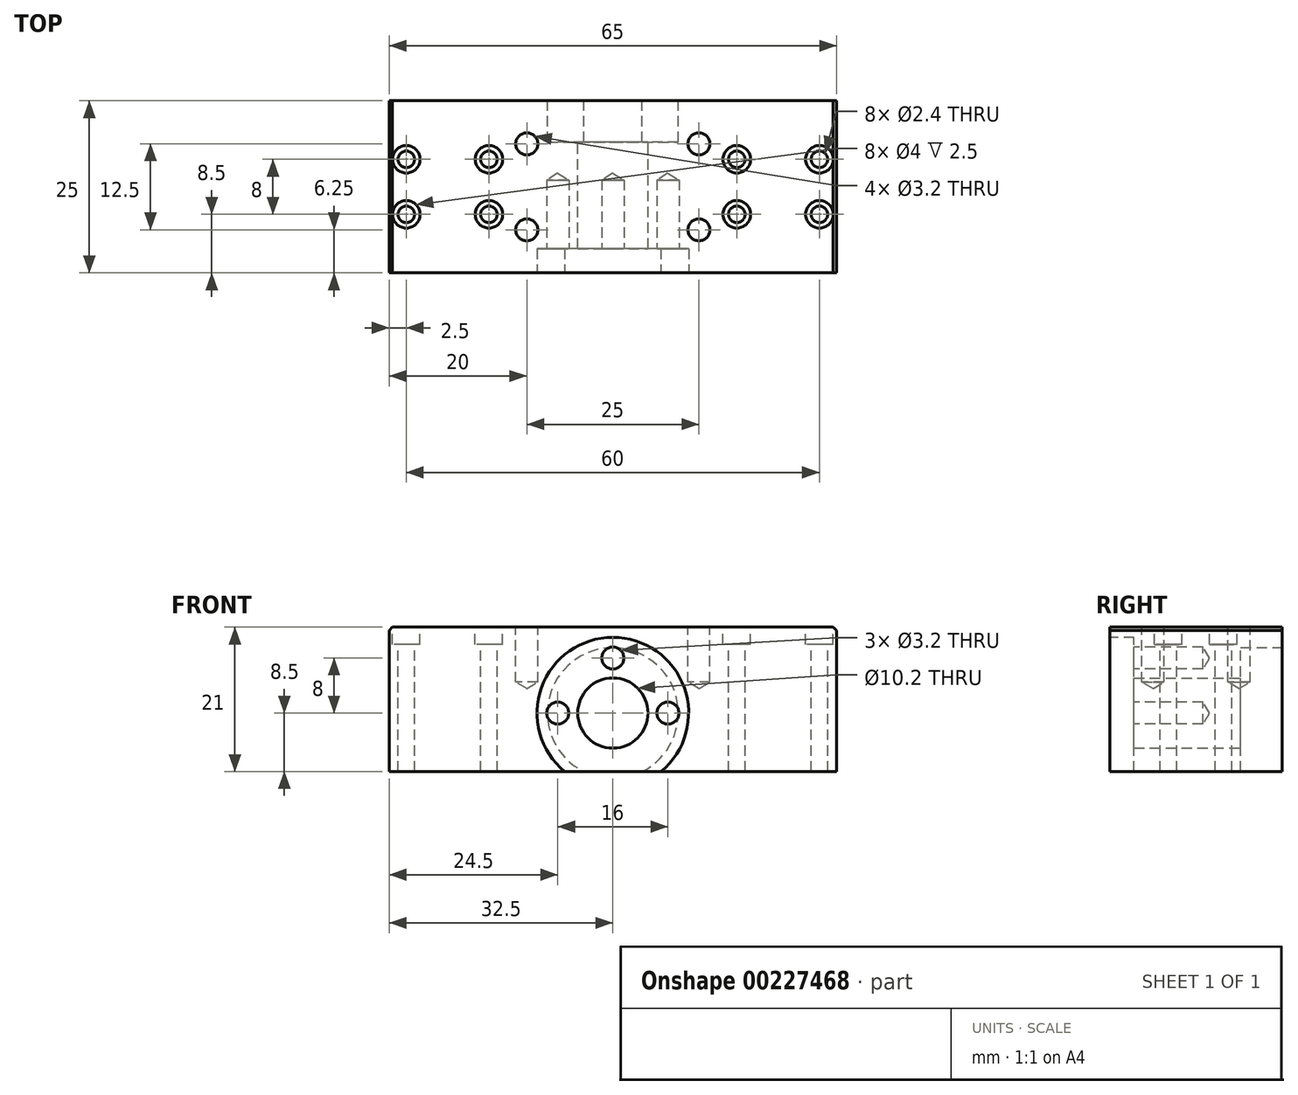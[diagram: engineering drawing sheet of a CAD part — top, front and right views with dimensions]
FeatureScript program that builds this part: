
annotation { "Feature Type Name" : "Feature", "Feature Type Description" : "" }
export const myFeature = defineFeature(function(context is Context, id is Id, definition is map)
    precondition{}
    {
        {
            var Q0;
            Q0=qCreatedBy(makeId("Front.planeOp"),FACE);
            var sketch = newSketch(context, id + "F0", { "sketchPlane" : qUnion([Q0])});
            skLineSegment(sketch, "E0.bottom", {"start": v(32.5, -8.5) * mm, "end": v(-32.5, -8.5) * mm});
            skLineSegment(sketch, "E0.top", {"start": v(32.5, 12.5) * mm, "end": v(-32.5, 12.5) * mm});
            skLineSegment(sketch, "E0.left", {"start": v(32.5, -8.5) * mm, "end": v(32.5, 12.5) * mm});
            skLineSegment(sketch, "E0.right", {"start": v(-32.5, -8.5) * mm, "end": v(-32.5, 12.5) * mm});
            skPoint(sketch, "E0.middle", {"position": v(0, 0) * mm});
            skCircle(sketch, "E1", {"center": v(0, 0) * mm, "radius": 5.1 * mm});
            skPoint(sketch, "E2", {"position": v(0, -8.5) * mm});
            skPoint(sketch, "E3", {"position": v(32.5, -7.5) * mm});
            skSolve(sketch);
        }
        {
            var Q0;
            {var subQ1=sQuery(id+"F0.wireOp",EDGE,"E0.top");Q0=makeQuery(id+"F0.imprint","IMPRINT",FACE,{"disambiguationData":[TD([[makeQuery(id+"F0.imprint","IMPRINT",EDGE,{"derivedFrom":subQ1}),1.0]])]});}
            extrude(context, id + "F1", {"entities" : qUnion([Q0]), "depth" : 25 * mm});
        }
        {
            var Q0;
            Q0=makeQuery(id+"F1.opExtrude","SWEPT_FACE",FACE,{"disambiguationData":[OSD([sQuery(id+"F0.wireOp",EDGE,"E0.top")])]});
            var sketch = newSketch(context, id + "F2", { "sketchPlane" : qUnion([Q0])});
            skPoint(sketch, "E4", {"position": v(-30, -8.5) * mm});
            skPoint(sketch, "E5.0.1.0", {"position": v(-30, -16.5) * mm});
            skPoint(sketch, "E5.1.0.0", {"position": v(-18, -8.5) * mm});
            skPoint(sketch, "E5.1.1.0", {"position": v(-18, -16.5) * mm});
            skLineSegment(sketch, "E5.direction1", {"start": v(-30, -8.5) * mm, "end": v(-18, -8.5) * mm, "construction": true});
            skLineSegment(sketch, "E5.direction2", {"start": v(-30, -8.5) * mm, "end": v(-30, -16.5) * mm, "construction": true});
            skPoint(sketch, "E6.MirrorP", {"position": v(30, -8.5) * mm});
            skPoint(sketch, "E7.MirrorP", {"position": v(18, -8.5) * mm});
            skPoint(sketch, "E8.MirrorP", {"position": v(18, -16.5) * mm});
            skPoint(sketch, "E9.MirrorP", {"position": v(30, -16.5) * mm});
            skSolve(sketch);
        }
        {
            var Q0;
            Q0=sQuery(id+"F2.wireOp",VERTEX,"E4");
            var Q1;
            Q1=sQuery(id+"F2.wireOp",VERTEX,"E5.0.1.0");
            var Q2;
            Q2=sQuery(id+"F2.wireOp",VERTEX,"E5.1.0.0");
            var Q3;
            Q3=sQuery(id+"F2.wireOp",VERTEX,"E5.1.1.0");
            var Q4;
            Q4=sQuery(id+"F2.wireOp",VERTEX,"E8.MirrorP");
            var Q5;
            Q5=sQuery(id+"F2.wireOp",VERTEX,"E7.MirrorP");
            var Q6;
            Q6=sQuery(id+"F2.wireOp",VERTEX,"E6.MirrorP");
            var Q7;
            Q7=sQuery(id+"F2.wireOp",VERTEX,"E9.MirrorP");
            var Q8;
            Q8=makeQuery(id+"F1.opExtrude","SWEPT_BODY",BODY,{"disambiguationData":[OSD([sQuery(id+"F0.wireOp",EDGE,"E0.bottom"),sQuery(id+"F0.wireOp",EDGE,"E0.top"),sQuery(id+"F0.wireOp",EDGE,"E0.left"),sQuery(id+"F0.wireOp",EDGE,"E0.right"),sQuery(id+"F0.wireOp",EDGE,"E1")])]});
            hole(context, id + "F3", {"style" : HoleStyle.C_BORE, "endStyle" : HoleEndStyle.THROUGH, "holeDiameter" : 2.4 * mm, "cBoreDiameter" : 4 * mm, "cBoreDepth" : 2.5 * mm, "locations" : qUnion([Q0, Q1, Q2, Q3, Q4, Q5, Q6, Q7]), "scope" : qUnion([Q8]), "tappedDepth" : 12 * mm, "tapClearance" : 3});
        }
        {
            var Q0;
            Q0=makeQuery(id+"F1.opExtrude","SWEPT_EDGE",EDGE,{"disambiguationData":[OSD([sQuery(id+"F0.wireOp",EDGE,"E0.top"),sQuery(id+"F0.wireOp",EDGE,"E0.right")])]});
            var Q1;
            Q1=makeQuery(id+"F1.opExtrude","SWEPT_EDGE",EDGE,{"disambiguationData":[OSD([sQuery(id+"F0.wireOp",EDGE,"E0.top"),sQuery(id+"F0.wireOp",EDGE,"E0.left")])]});
            chamfer(context, id + "F4", {"entities" : qUnion([Q0, Q1]), "width" : 0.5 * mm, "tangentPropagation" : true});
        }
        {
            var Q0;
            Q0=makeQuery(id+"F1.opExtrude","CAP_FACE",FACE,{"disambiguationData":[OSD([sQuery(id+"F0.wireOp",EDGE,"E0.bottom"),sQuery(id+"F0.wireOp",EDGE,"E0.top"),sQuery(id+"F0.wireOp",EDGE,"E0.left"),sQuery(id+"F0.wireOp",EDGE,"E0.right"),sQuery(id+"F0.wireOp",EDGE,"E1")])],"isStart":false});
            var sketch = newSketch(context, id + "F5", { "sketchPlane" : qUnion([Q0])});
            skCircle(sketch, "E10", {"center": v(0, 0) * mm, "radius": 11 * mm});
            skSolve(sketch);
        }
        {
            var Q0;
            Q0=makeQuery(id+"F5.imprint","IMPRINT",FACE,{"disambiguationData":[TD([[makeQuery(id+"F5.imprint","IMPRINT",EDGE,{"derivedFrom":makeQuery(id+"F1.opExtrude","CAP_EDGE",EDGE,{"disambiguationData":[OSD([sQuery(id+"F0.wireOp",EDGE,"E1")])],"isStart":false})}),-1.0]])]});
            extrude(context, id + "F6", {"entities" : qUnion([Q0]), "operationType" : NewBodyOperationType.REMOVE, "oppositeDirection" : true, "depth" : 3.5 * mm});
        }
        {
            var Q0;
            Q0=makeQuery(id+"F1.opExtrude","SWEPT_FACE",FACE,{"disambiguationData":[OSD([sQuery(id+"F0.wireOp",EDGE,"E0.top")])]});
            var sketch = newSketch(context, id + "F7", { "sketchPlane" : qUnion([Q0])});
            skPoint(sketch, "E11", {"position": v(12.5, -6.25) * mm});
            skPoint(sketch, "E12.0.1.0", {"position": v(12.5, -18.75) * mm});
            skPoint(sketch, "E12.1.0.0", {"position": v(-12.5, -6.25) * mm});
            skPoint(sketch, "E12.1.1.0", {"position": v(-12.5, -18.75) * mm});
            skLineSegment(sketch, "E12.direction1", {"start": v(12.5, -6.25) * mm, "end": v(-12.5, -6.25) * mm, "construction": true});
            skLineSegment(sketch, "E12.direction2", {"start": v(12.5, -6.25) * mm, "end": v(12.5, -18.75) * mm, "construction": true});
            skSolve(sketch);
        }
        {
            var Q0;
            Q0=sQuery(id+"F7.wireOp",VERTEX,"E11");
            var Q1;
            Q1=sQuery(id+"F7.wireOp",VERTEX,"E12.0.1.0");
            var Q2;
            Q2=sQuery(id+"F7.wireOp",VERTEX,"E12.1.0.0");
            var Q3;
            Q3=sQuery(id+"F7.wireOp",VERTEX,"E12.1.1.0");
            var Q4;
            Q4=makeQuery(id+"F1.opExtrude","SWEPT_BODY",BODY,{"disambiguationData":[OSD([sQuery(id+"F0.wireOp",EDGE,"E0.bottom"),sQuery(id+"F0.wireOp",EDGE,"E0.top"),sQuery(id+"F0.wireOp",EDGE,"E0.left"),sQuery(id+"F0.wireOp",EDGE,"E0.right"),sQuery(id+"F0.wireOp",EDGE,"E1")])]});
            hole(context, id + "F8", {"style" : HoleStyle.SIMPLE, "endStyle" : HoleEndStyle.BLIND, "standardTappedOrClearance" : lookupTablePath({ "standard" : "ISO", "engagement" : "75%", "pitch" : "0.75 mm", "size" : "M4", "type" : "Tapped" }), "standardBlindInLast" : lookupTablePath({ "standard" : "ISO", "engagement" : "75%", "pitch" : "0.75 mm", "size" : "M4", "type" : "Tapped" }), "holeDiameter" : 3.2 * mm, "holeDepth" : 8 * mm, "locations" : qUnion([Q0, Q1, Q2, Q3]), "scope" : qUnion([Q4])});
        }
        {
            var Q0;
            Q0=makeQuery(id+"F6.boolean.opBoolean","COPY",FACE,{"derivedFrom":makeQuery(id+"F6.opExtrude","CAP_FACE",FACE,{"disambiguationData":[OSD([sQuery(id+"F0.wireOp",EDGE,"E0.bottom"),sQuery(id+"F0.wireOp",EDGE,"E1"),sQuery(id+"F5.wireOp",EDGE,"E10")])],"isStart":false})});
            var sketch = newSketch(context, id + "F9", { "sketchPlane" : qUnion([Q0])});
            skCircle(sketch, "E13", {"center": v(0, 0) * mm, "radius": 8 * mm, "construction": true});
            skPoint(sketch, "E14", {"position": v(0, 8) * mm});
            skPoint(sketch, "E15.1.0", {"position": v(-8, 0) * mm});
            skPoint(sketch, "E15.2.0", {"position": v(0, -8) * mm});
            skPoint(sketch, "E16.0.3.0", {"position": v(8, 0) * mm});
            skSolve(sketch);
        }
        {
            var Q0;
            Q0=sQuery(id+"F9.wireOp",VERTEX,"E15.1.0");
            var Q1;
            Q1=sQuery(id+"F9.wireOp",VERTEX,"E14");
            var Q2;
            Q2=sQuery(id+"F9.wireOp",VERTEX,"E16.0.3.0");
            var Q3;
            Q3=makeQuery(id+"F1.opExtrude","SWEPT_BODY",BODY,{"disambiguationData":[OSD([sQuery(id+"F0.wireOp",EDGE,"E0.bottom"),sQuery(id+"F0.wireOp",EDGE,"E0.top"),sQuery(id+"F0.wireOp",EDGE,"E0.left"),sQuery(id+"F0.wireOp",EDGE,"E0.right"),sQuery(id+"F0.wireOp",EDGE,"E1")])]});
            hole(context, id + "F10", {"style" : HoleStyle.SIMPLE, "endStyle" : HoleEndStyle.BLIND, "standardTappedOrClearance" : lookupTablePath({ "standard" : "ISO", "engagement" : "75%", "pitch" : "0.75 mm", "size" : "M4", "type" : "Tapped" }), "standardBlindInLast" : lookupTablePath({ "standard" : "ISO", "engagement" : "75%", "pitch" : "0.75 mm", "size" : "M4", "type" : "Tapped" }), "holeDiameter" : 3.2 * mm, "holeDepth" : 10 * mm, "locations" : qUnion([Q0, Q1, Q2]), "scope" : qUnion([Q3]), "tappedDepth" : 12 * mm, "tapClearance" : 3});
        }
        {
            var Q0;
            Q0=makeQuery(id+"F1.opExtrude","CAP_FACE",FACE,{"disambiguationData":[OSD([sQuery(id+"F0.wireOp",EDGE,"E0.bottom"),sQuery(id+"F0.wireOp",EDGE,"E0.top"),sQuery(id+"F0.wireOp",EDGE,"E0.left"),sQuery(id+"F0.wireOp",EDGE,"E0.right"),sQuery(id+"F0.wireOp",EDGE,"E1")])],"isStart":true});
            var sketch = newSketch(context, id + "F11", { "sketchPlane" : qUnion([Q0])});
            skCircle(sketch, "E17", {"center": v(0, 0) * mm, "radius": 9.5 * mm});
            skSolve(sketch);
        }
        {
            var Q0;
            Q0=makeQuery(id+"F11.imprint","IMPRINT",FACE,{"disambiguationData":[TD([[makeQuery(id+"F11.imprint","IMPRINT",EDGE,{"derivedFrom":makeQuery(id+"F1.opExtrude","CAP_EDGE",EDGE,{"disambiguationData":[OSD([sQuery(id+"F0.wireOp",EDGE,"E1")])],"isStart":true})}),1.0]])]});
            extrude(context, id + "F12", {"entities" : qUnion([Q0]), "operationType" : NewBodyOperationType.REMOVE, "oppositeDirection" : true, "depth" : 6 * mm});
        }
    });
